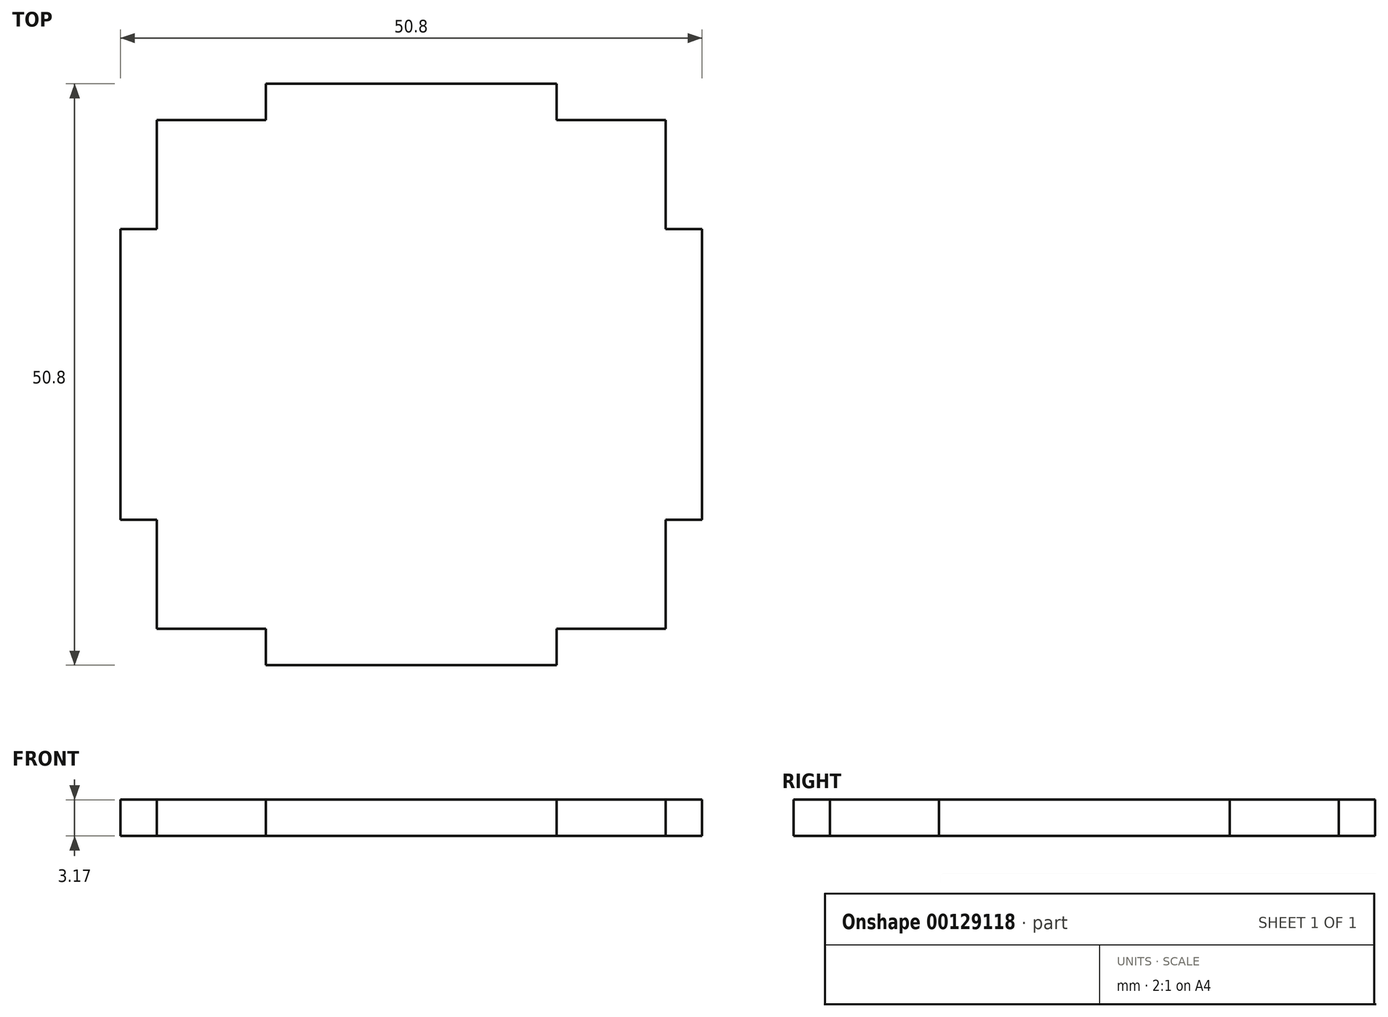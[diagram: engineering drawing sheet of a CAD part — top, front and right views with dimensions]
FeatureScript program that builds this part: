
annotation { "Feature Type Name" : "Feature", "Feature Type Description" : "" }
export const myFeature = defineFeature(function(context is Context, id is Id, definition is map)
    precondition{}
    {
        {
            var Q0;
            Q0=qCreatedBy(makeId("Top.planeOp"),FACE);
            var sketch = newSketch(context, id + "F0", { "sketchPlane" : qUnion([Q0])});
            skLineSegment(sketch, "E0.bottom", {"start": v(-25.4, 25.4) * mm, "end": v(25.4, 25.4) * mm});
            skLineSegment(sketch, "E0.top", {"start": v(-25.4, -25.4) * mm, "end": v(25.4, -25.4) * mm});
            skLineSegment(sketch, "E0.left", {"start": v(-25.4, 25.4) * mm, "end": v(-25.4, -25.4) * mm});
            skLineSegment(sketch, "E0.right", {"start": v(25.4, 25.4) * mm, "end": v(25.4, -25.4) * mm});
            skPoint(sketch, "E0.middle", {"position": v(0, 0) * mm});
            skLineSegment(sketch, "E1", {"start": v(-25.4, 25.4) * mm, "end": v(-22.23, 25.4) * mm});
            skLineSegment(sketch, "E2.0.1.0", {"start": v(-25.4, 12.7) * mm, "end": v(-22.23, 12.7) * mm});
            skLineSegment(sketch, "E2.0.2.0", {"start": v(-25.4, 0) * mm, "end": v(-22.23, 0) * mm});
            skLineSegment(sketch, "E2.0.3.0", {"start": v(-25.4, -12.7) * mm, "end": v(-22.23, -12.7) * mm});
            skLineSegment(sketch, "E2.0.4.0", {"start": v(-25.4, -25.4) * mm, "end": v(-22.23, -25.4) * mm});
            skLineSegment(sketch, "E2.direction1", {"start": v(-25.4, 25.4) * mm, "end": v(0, 25.4) * mm, "construction": true});
            skLineSegment(sketch, "E2.direction2", {"start": v(-25.4, 25.4) * mm, "end": v(-25.4, 12.7) * mm, "construction": true});
            skLineSegment(sketch, "E3", {"start": v(-22.23, 25.4) * mm, "end": v(-22.23, -25.4) * mm});
            skLineSegment(sketch, "E4.MirrorCS", {"start": v(25.4, 25.4) * mm, "end": v(22.23, 25.4) * mm});
            skLineSegment(sketch, "E5.MirrorCS", {"start": v(25.4, -25.4) * mm, "end": v(22.23, -25.4) * mm});
            skLineSegment(sketch, "E6.MirrorCS", {"start": v(25.4, 12.7) * mm, "end": v(22.23, 12.7) * mm});
            skLineSegment(sketch, "E7.MirrorCS", {"start": v(25.4, 0) * mm, "end": v(22.23, 0) * mm});
            skLineSegment(sketch, "E8.MirrorCS", {"start": v(25.4, -12.7) * mm, "end": v(22.23, -12.7) * mm});
            skLineSegment(sketch, "E9.MirrorCS", {"start": v(22.23, 25.4) * mm, "end": v(22.23, -25.4) * mm});
            skLineSegment(sketch, "E10.MirrorCS", {"start": v(25.4, 25.4) * mm, "end": v(25.4, 12.7) * mm, "construction": true});
            skLineSegment(sketch, "E11", {"start": v(-25.4, 25.4) * mm, "end": v(-25.4, 22.23) * mm});
            skLineSegment(sketch, "E12.1.0.0", {"start": v(-12.7, 25.4) * mm, "end": v(-12.7, 22.23) * mm});
            skLineSegment(sketch, "E12.2.0.0", {"start": v(0, 25.4) * mm, "end": v(0, 22.23) * mm});
            skLineSegment(sketch, "E12.3.0.0", {"start": v(12.7, 25.4) * mm, "end": v(12.7, 22.23) * mm});
            skLineSegment(sketch, "E12.4.0.0", {"start": v(25.4, 25.4) * mm, "end": v(25.4, 22.23) * mm});
            skLineSegment(sketch, "E12.direction1", {"start": v(-25.4, 22.23) * mm, "end": v(-12.7, 22.23) * mm, "construction": true});
            skLineSegment(sketch, "E13", {"start": v(-25.4, 22.23) * mm, "end": v(25.4, 22.23) * mm});
            skLineSegment(sketch, "E14.MirrorCS", {"start": v(-25.4, -25.4) * mm, "end": v(-25.4, -22.23) * mm});
            skLineSegment(sketch, "E15.MirrorCS", {"start": v(25.4, -25.4) * mm, "end": v(25.4, -22.23) * mm});
            skLineSegment(sketch, "E16.MirrorCS", {"start": v(-12.7, -25.4) * mm, "end": v(-12.7, -22.23) * mm});
            skLineSegment(sketch, "E17.MirrorCS", {"start": v(12.7, -25.4) * mm, "end": v(12.7, -22.23) * mm});
            skLineSegment(sketch, "E18.MirrorCS", {"start": v(0, -25.4) * mm, "end": v(0, -22.23) * mm});
            skLineSegment(sketch, "E19.MirrorCS", {"start": v(-25.4, -22.23) * mm, "end": v(25.4, -22.23) * mm});
            skLineSegment(sketch, "E20.MirrorCS", {"start": v(-25.4, -25.4) * mm, "end": v(0, -25.4) * mm, "construction": true});
            skLineSegment(sketch, "E21.MirrorCS", {"start": v(-25.4, -22.23) * mm, "end": v(-12.7, -22.23) * mm, "construction": true});
            skSolve(sketch);
        }
        {
            var Q0;
            {var subQ7=sQuery(id+"F0.wireOp",EDGE,"E3");var subQ11=makeQuery(id+"F0.imprint","INTERSECT",VERTEX,{"derivedFrom":[sQuery(id+"F0.wireOp",EDGE,"E2.0.1.0"),subQ7]});Q0=makeQuery(id+"F0.imprint","IMPRINT",FACE,{"disambiguationData":[TD([[makeQuery(id+"F0.imprint","IMPRINT",EDGE,{"disambiguationData":[TD([[subQ11,1.0]])],"derivedFrom":subQ7}),1.0]])]});}
            var Q1;
            {var subQ0=sQuery(id+"F0.wireOp",EDGE,"E12.1.0.0");Q1=makeQuery(id+"F0.imprint","IMPRINT",FACE,{"disambiguationData":[TD([[makeQuery(id+"F0.imprint","IMPRINT",EDGE,{"derivedFrom":subQ0}),1.0]])]});}
            var Q2;
            {var subQ0=sQuery(id+"F0.wireOp",EDGE,"E12.2.0.0");Q2=makeQuery(id+"F0.imprint","IMPRINT",FACE,{"disambiguationData":[TD([[makeQuery(id+"F0.imprint","IMPRINT",EDGE,{"derivedFrom":subQ0}),1.0]])]});}
            var Q3;
            {var subQ0=sQuery(id+"F0.wireOp",EDGE,"E6.MirrorCS");Q3=makeQuery(id+"F0.imprint","IMPRINT",FACE,{"disambiguationData":[TD([[makeQuery(id+"F0.imprint","IMPRINT",EDGE,{"derivedFrom":subQ0}),1.0]])]});}
            var Q4;
            {var subQ0=sQuery(id+"F0.wireOp",EDGE,"E7.MirrorCS");Q4=makeQuery(id+"F0.imprint","IMPRINT",FACE,{"disambiguationData":[TD([[makeQuery(id+"F0.imprint","IMPRINT",EDGE,{"derivedFrom":subQ0}),1.0]])]});}
            var Q5;
            {var subQ0=sQuery(id+"F0.wireOp",EDGE,"E17.MirrorCS");Q5=makeQuery(id+"F0.imprint","IMPRINT",FACE,{"disambiguationData":[TD([[makeQuery(id+"F0.imprint","IMPRINT",EDGE,{"derivedFrom":subQ0}),1.0]])]});}
            var Q6;
            {var subQ0=sQuery(id+"F0.wireOp",EDGE,"E16.MirrorCS");Q6=makeQuery(id+"F0.imprint","IMPRINT",FACE,{"disambiguationData":[TD([[makeQuery(id+"F0.imprint","IMPRINT",EDGE,{"derivedFrom":subQ0}),-1.0]])]});}
            var Q7;
            {var subQ0=sQuery(id+"F0.wireOp",EDGE,"E2.0.2.0");Q7=makeQuery(id+"F0.imprint","IMPRINT",FACE,{"disambiguationData":[TD([[makeQuery(id+"F0.imprint","IMPRINT",EDGE,{"derivedFrom":subQ0}),-1.0]])]});}
            var Q8;
            {var subQ0=sQuery(id+"F0.wireOp",EDGE,"E2.0.1.0");Q8=makeQuery(id+"F0.imprint","IMPRINT",FACE,{"disambiguationData":[TD([[makeQuery(id+"F0.imprint","IMPRINT",EDGE,{"derivedFrom":subQ0}),-1.0]])]});}
            extrude(context, id + "F1", {"entities" : qUnion([Q0, Q1, Q2, Q3, Q4, Q5, Q6, Q7, Q8]), "depth" : 3.17 * mm});
        }
    });
